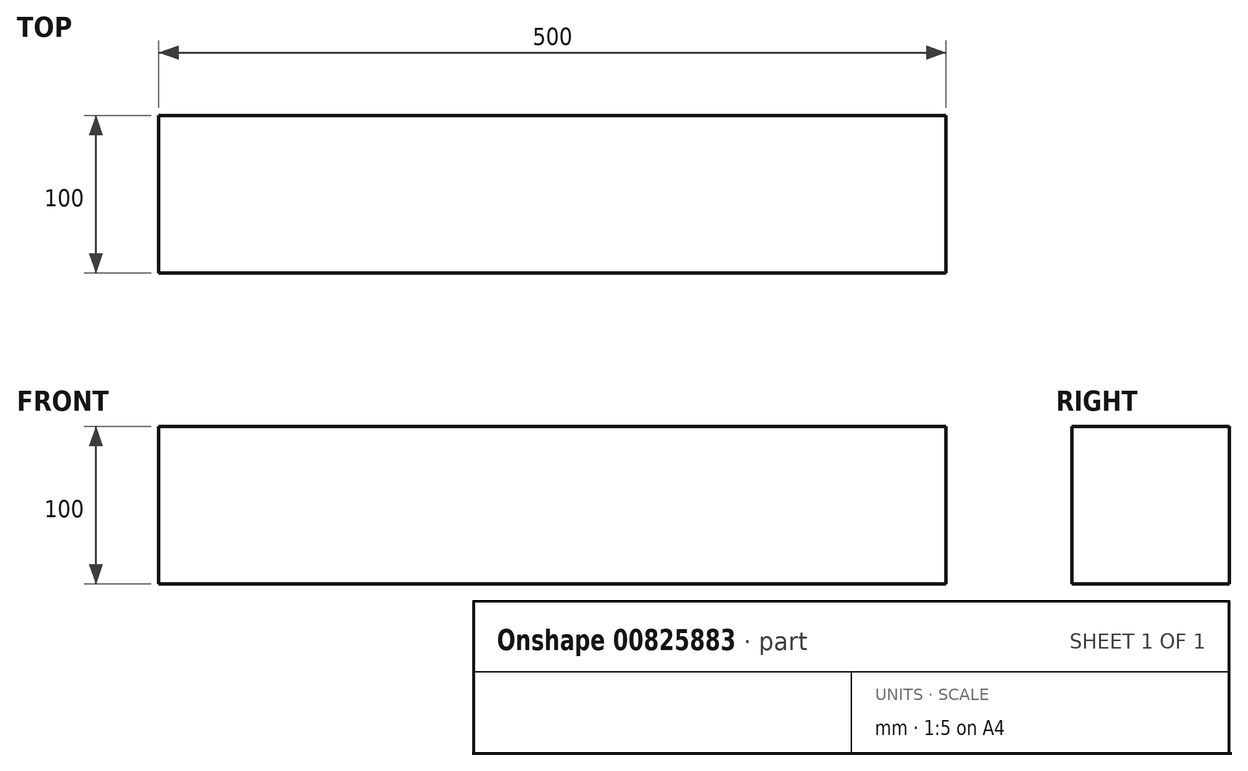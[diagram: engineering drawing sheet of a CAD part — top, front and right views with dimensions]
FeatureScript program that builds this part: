
annotation { "Feature Type Name" : "Feature", "Feature Type Description" : "" }
export const myFeature = defineFeature(function(context is Context, id is Id, definition is map)
    precondition{}
    {
        {
            var Q0;
            Q0=qCreatedBy(makeId("Top.planeOp"),FACE);
            var sketch = newSketch(context, id + "F0", { "sketchPlane" : qUnion([Q0])});
            skLineSegment(sketch, "E0.bottom", {"start": v(250, -50) * mm, "end": v(-250, -50) * mm});
            skLineSegment(sketch, "E0.top", {"start": v(250, 50) * mm, "end": v(-250, 50) * mm});
            skLineSegment(sketch, "E0.left", {"start": v(250, -50) * mm, "end": v(250, 50) * mm});
            skLineSegment(sketch, "E0.right", {"start": v(-250, -50) * mm, "end": v(-250, 50) * mm});
            skPoint(sketch, "E0.middle", {"position": v(0, 0) * mm});
            skSolve(sketch);
        }
        {
            var Q0;
            Q0=makeQuery(id+"F0.imprint","IMPRINT",FACE,{"disambiguationData":[TD([[makeQuery(id+"F0.imprint","IMPRINT",EDGE,{"derivedFrom":sQuery(id+"F0.wireOp",EDGE,"E0.bottom")}),-1.0]])]});
            extrude(context, id + "F1", {"entities" : qUnion([Q0]), "depth" : 100 * mm, "offsetDistance" : 25 * mm});
        }
    });
